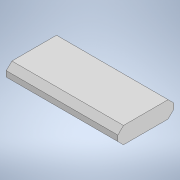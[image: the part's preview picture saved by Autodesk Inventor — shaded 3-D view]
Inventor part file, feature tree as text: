
AUTODESK INVENTOR PART (.ipt)
format: ipt  version: 2022.3 (Build 263350000, 350)  size: 98,816 bytes
history: native  units: mm
features: extrude x1, chamfer x1, sketch x1
ambient origin geometry x8: Origin, YZ Plane, XZ Plane, XY Plane, X Axis, Y Axis, Z Axis, Center Point
bodies: Solid1 (feature_tree)
feature tree (3):
  extrude  "Extrusion1"  Depth=10.0mm
  chamfer  "Chamfer1"  Distance=3.0mm
  sketch  "Sketch1"  dims[d0=20.0mm d1=10.0mm d2=3.0mm d3=0.0mm d4=1.0mm d5=2.0mm d6=45.0deg]
